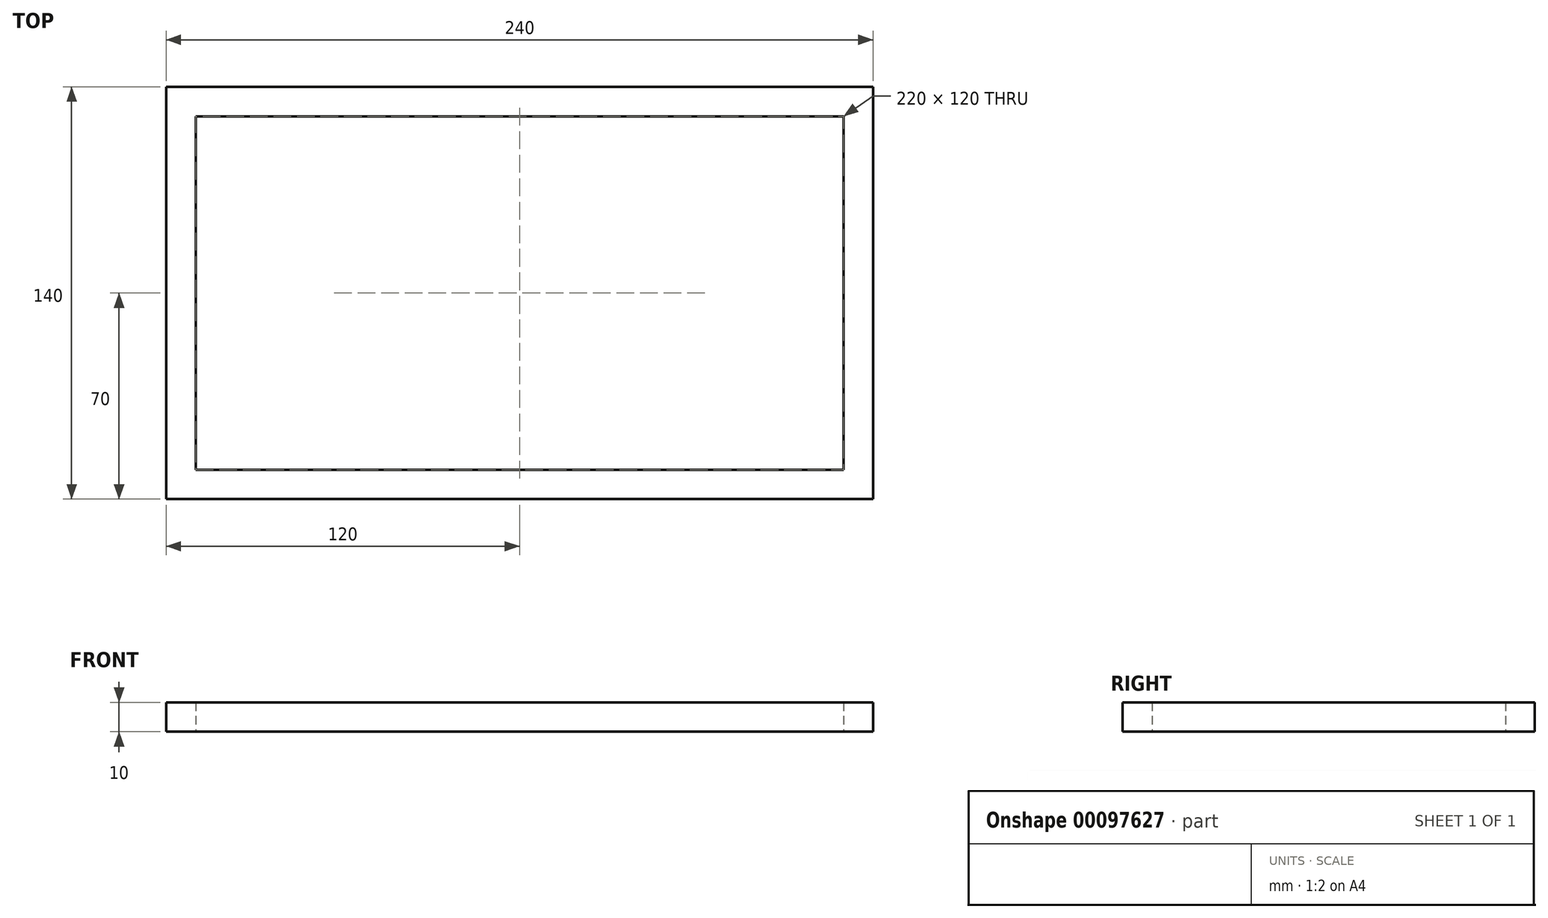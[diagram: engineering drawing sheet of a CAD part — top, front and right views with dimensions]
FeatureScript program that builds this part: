
annotation { "Feature Type Name" : "Feature", "Feature Type Description" : "" }
export const myFeature = defineFeature(function(context is Context, id is Id, definition is map)
    precondition{}
    {
        {
            var Q0;
            Q0=qCreatedBy(makeId("Top.planeOp"),FACE);
            var sketch = newSketch(context, id + "F0", { "sketchPlane" : qUnion([Q0])});
            skLineSegment(sketch, "E0.bottom", {"start": v(120, -70) * mm, "end": v(-120, -70) * mm});
            skLineSegment(sketch, "E0.top", {"start": v(120, 70) * mm, "end": v(-120, 70) * mm});
            skLineSegment(sketch, "E0.left", {"start": v(120, -70) * mm, "end": v(120, 70) * mm});
            skLineSegment(sketch, "E0.right", {"start": v(-120, -70) * mm, "end": v(-120, 70) * mm});
            skPoint(sketch, "E0.middle", {"position": v(0, 0) * mm});
            skLineSegment(sketch, "E1.0", {"start": v(110, 60) * mm, "end": v(-110, 60) * mm});
            skLineSegment(sketch, "E1.1", {"start": v(110, -60) * mm, "end": v(110, 60) * mm});
            skLineSegment(sketch, "E1.2", {"start": v(110, -60) * mm, "end": v(-110, -60) * mm});
            skLineSegment(sketch, "E1.3", {"start": v(-110, -60) * mm, "end": v(-110, 60) * mm});
            skSolve(sketch);
        }
        {
            var Q0;
            Q0=makeQuery(id+"F0.imprint","IMPRINT",FACE,{"disambiguationData":[TD([[makeQuery(id+"F0.imprint","IMPRINT",EDGE,{"derivedFrom":sQuery(id+"F0.wireOp",EDGE,"E0.bottom")}),-1.0]])]});
            extrude(context, id + "F1", {"entities" : qUnion([Q0]), "depth" : 10 * mm});
        }
    });
